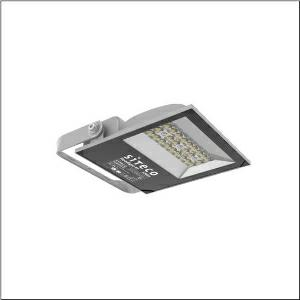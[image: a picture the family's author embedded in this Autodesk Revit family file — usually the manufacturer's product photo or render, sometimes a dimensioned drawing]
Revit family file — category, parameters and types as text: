
# Revit family: floodlight_fl_41_mini___pl32_5xa8571a2121_f875
name_source: partatom
category: Lighting Fixtures
units: mm (PartAtom-declared; Revit-internal decimal feet)

## family parameters
Cut with Voids When Loaded = No
Host = Face
Light Source = No
Part Type = Normal
Room Calculation Point = No
Round Connector Dimension = Use Diameter
Shared = No

## types (1)
- --- (1 x LED, 13000 lm, 100 W, 4000K)
    Apparent Load = 100 VA
    CIE Flux Codes = 40 79 99 100 100
    Color Rendering = 70
    Color Temperature = 4000K
    Default Elevation = 1800 mm
    Description = Floodlight FL 41 mini, floodlight, primary light control with lens, of PMMA, primary optical cover: protective disc, transparent, light distribution: PL32, light emission: direct distribution, installation type: surface-mounted, LED, High Power LED, rated luminous flux: 13.000lm, luminous efficacy: 130lm/W, light colour: 740, colour temperature: 4000K, control gear: ON/OFF Multilumen, with cable, 3x 1.5mm², mains connection: 220..240V, AC, 50/60Hz, connection cable pre-assembled, cable length: 2m, rated input power: 100W, luminaire housing, of diecast aluminium, powder-coated, metallic grey (RAL 9006), length: 265mm, width: 245mm, height: 54mm, protection rating (complete): IP65, insulation class (complete): insulation class I (protective earthing), certification: CE, ENEC, impact resistance: IK08, permissible operating ambient temperature: -40..+40°C, permissible storage temperature: -40..+60°C, packaging unit: 1 piece

Light Distribution: PL32
    Height = 54 mm
    Lamp = 1 x LED
    Lamp Light Flux = 13000 lm
    Lamp Power = 100 W
    Lamp count = 1
    Length = 226 mm
    Luminous efficacy = 130 lm/W
    Manufacturer = Siteco
    ModVariant = No
    Model = 5XA8571A2121
    Mounting Place = Ceiling
    Mounting Type = Surface mounted
    Number of Poles = 1
    OnlyDefault = Yes
    Power Factor = 1
    Product Name = Floodlight FL 41 mini | PL32
    Product group = floodlight | ceiling mounted
    ProductGroupID = 301
    Protection Class = Protection class I
    Protection Degree = IP 65
    RLX_Detail_Level = 1
    RLX_Emergency_Light_Flux = 0 lm
    RLX_Emergency_Type = 0
    RLX_Emergency_Type_DB = No
    RlxData = <blob elided: 24629 chars, md5=81b2d931>
    Socket = socket
    Standby Power = 0 W
    System Light Flux = 13000 lm
    System Power = 100 W
    Type Comments = factory setting: luminous flux: 100 % | (OFF | OFF | OFF)
    Type Image = l_1248226.jpg
    URL = http://relux.com
    VarID = @adj_131672
    Voltage = 0 V
    Weight = 0.00 kg
    Width = 241 mm

## geometry (parser evidence)
native form markers: Blend x4, Sweep x9
no freeform markers — native parametric forms only
